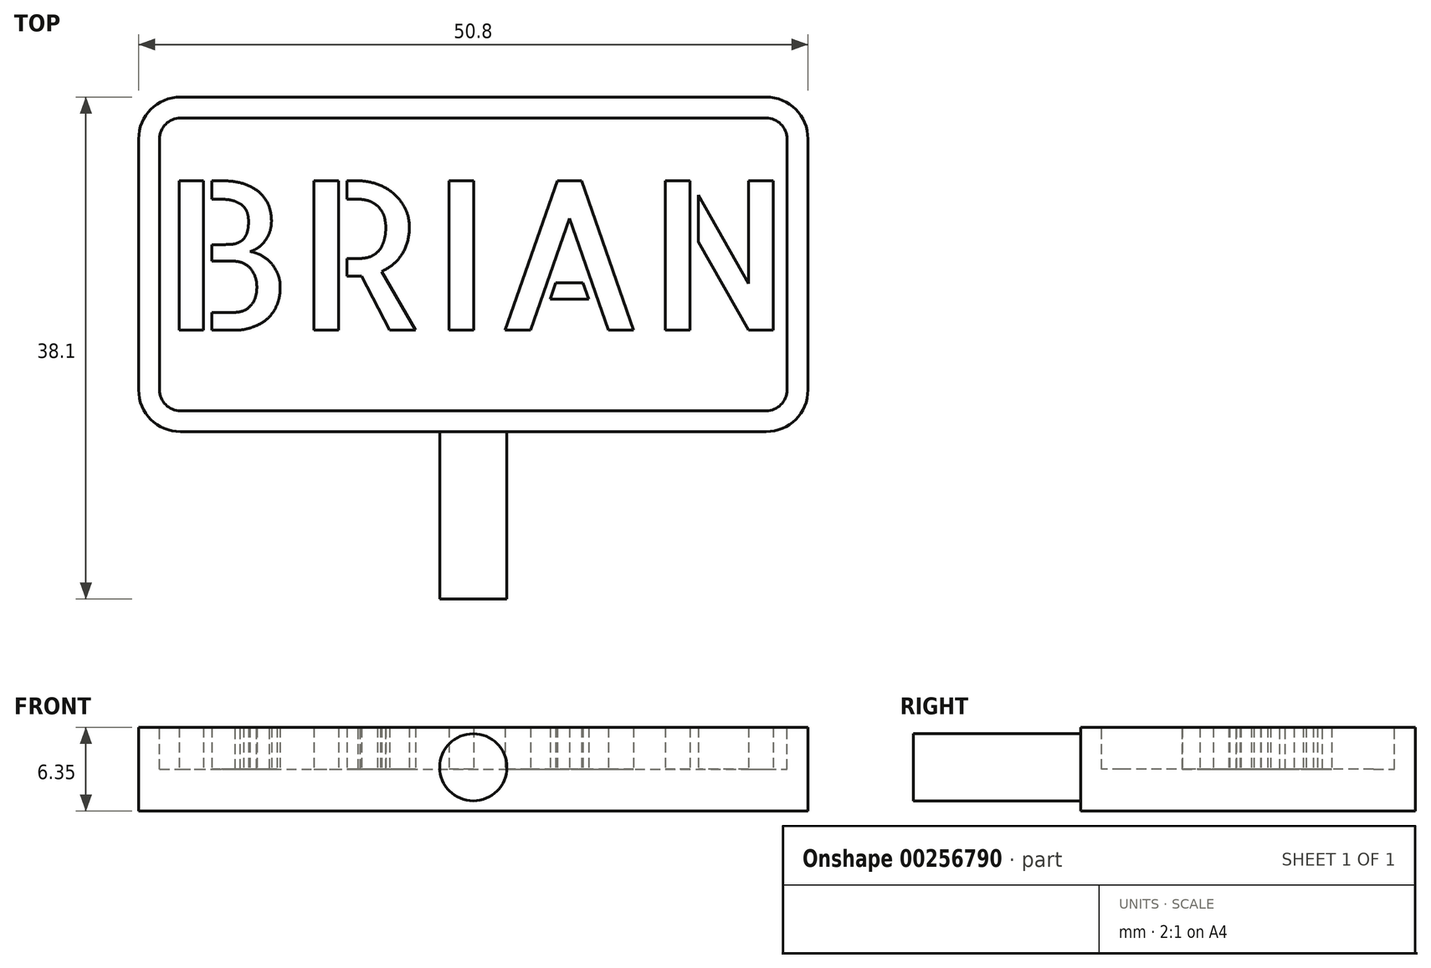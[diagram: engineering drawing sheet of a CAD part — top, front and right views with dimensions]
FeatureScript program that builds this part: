
annotation { "Feature Type Name" : "Feature", "Feature Type Description" : "" }
export const myFeature = defineFeature(function(context is Context, id is Id, definition is map)
    precondition{}
    {
        {
            var Q0;
            Q0=qCreatedBy(makeId("Top.planeOp"),FACE);
            var sketch = newSketch(context, id + "F0", { "sketchPlane" : qUnion([Q0])});
            skLineSegment(sketch, "E0.bottom", {"start": v(22.23, 12.7) * mm, "end": v(-22.23, 12.7) * mm});
            skLineSegment(sketch, "E0.top", {"start": v(22.23, -12.7) * mm, "end": v(-22.23, -12.7) * mm});
            skLineSegment(sketch, "E0.left", {"start": v(25.4, 9.53) * mm, "end": v(25.4, -9.53) * mm});
            skLineSegment(sketch, "E0.right", {"start": v(-25.4, 9.53) * mm, "end": v(-25.4, -9.53) * mm});
            skPoint(sketch, "E0.middle", {"position": v(0, 0) * mm});
            skPoint(sketch, "E1.visualSharp", {"position": v(-25.4, -12.7) * mm});
            skArc(sketch, "E1.filletArc", {"start": v(-25.4, -9.53) * mm, "mid": v(-24.47, -11.77) * mm, "end": v(-22.23, -12.7) * mm});
            skPoint(sketch, "E2.visualSharp", {"position": v(-25.4, 12.7) * mm});
            skArc(sketch, "E2.filletArc", {"start": v(-22.23, 12.7) * mm, "mid": v(-24.47, 11.77) * mm, "end": v(-25.4, 9.53) * mm});
            skPoint(sketch, "E3.visualSharp", {"position": v(25.4, 12.7) * mm});
            skArc(sketch, "E3.filletArc", {"start": v(25.4, 9.53) * mm, "mid": v(24.47, 11.77) * mm, "end": v(22.23, 12.7) * mm});
            skPoint(sketch, "E4.visualSharp", {"position": v(25.4, -12.7) * mm});
            skArc(sketch, "E4.filletArc", {"start": v(22.23, -12.7) * mm, "mid": v(24.47, -11.77) * mm, "end": v(25.4, -9.53) * mm});
            skSolve(sketch);
        }
        {
            var Q0;
            Q0=makeQuery(id+"F0.imprint","IMPRINT",FACE,{"disambiguationData":[TD([[makeQuery(id+"F0.imprint","IMPRINT",EDGE,{"derivedFrom":sQuery(id+"F0.wireOp",EDGE,"E0.bottom")}),1.0]])]});
            extrude(context, id + "F1", {"entities" : qUnion([Q0]), "depth" : 6.35 * mm});
        }
        {
            var Q0;
            Q0=makeQuery(id+"F1.opExtrude","CAP_FACE",FACE,{"disambiguationData":[OSD([sQuery(id+"F0.wireOp",EDGE,"E0.bottom"),sQuery(id+"F0.wireOp",EDGE,"E0.top"),sQuery(id+"F0.wireOp",EDGE,"E0.left"),sQuery(id+"F0.wireOp",EDGE,"E0.right"),sQuery(id+"F0.wireOp",EDGE,"E1.filletArc"),sQuery(id+"F0.wireOp",EDGE,"E2.filletArc"),sQuery(id+"F0.wireOp",EDGE,"E3.filletArc"),sQuery(id+"F0.wireOp",EDGE,"E4.filletArc")])],"isStart":false});
            var sketch = newSketch(context, id + "F2", { "sketchPlane" : qUnion([Q0])});
            skLineSegment(sketch, "E5.0", {"start": v(-22.22, -11.11) * mm, "end": v(22.22, -11.11) * mm});
            skLineSegment(sketch, "E5.1", {"start": v(-23.81, 9.52) * mm, "end": v(-23.81, -9.52) * mm});
            skLineSegment(sketch, "E5.2", {"start": v(22.22, 11.11) * mm, "end": v(-22.22, 11.11) * mm});
            skLineSegment(sketch, "E5.3", {"start": v(23.81, -9.52) * mm, "end": v(23.81, 9.52) * mm});
            skPoint(sketch, "E6.visualSharp", {"position": v(-23.81, 11.11) * mm});
            skArc(sketch, "E6.filletArc", {"start": v(-22.22, 11.11) * mm, "mid": v(-23.35, 10.65) * mm, "end": v(-23.81, 9.52) * mm});
            skPoint(sketch, "E7.visualSharp", {"position": v(-23.81, -11.11) * mm});
            skArc(sketch, "E7.filletArc", {"start": v(-23.81, -9.52) * mm, "mid": v(-23.35, -10.65) * mm, "end": v(-22.22, -11.11) * mm});
            skPoint(sketch, "E8.visualSharp", {"position": v(23.81, -11.11) * mm});
            skArc(sketch, "E8.filletArc", {"start": v(22.22, -11.11) * mm, "mid": v(23.35, -10.65) * mm, "end": v(23.81, -9.52) * mm});
            skPoint(sketch, "E9.visualSharp", {"position": v(23.81, 11.11) * mm});
            skArc(sketch, "E9.filletArc", {"start": v(23.81, 9.52) * mm, "mid": v(23.35, 10.65) * mm, "end": v(22.22, 11.11) * mm});
            skSolve(sketch);
        }
        {
            var Q0;
            Q0=makeQuery(id+"F2.imprint","IMPRINT",FACE,{"disambiguationData":[TD([[makeQuery(id+"F2.imprint","IMPRINT",EDGE,{"derivedFrom":sQuery(id+"F2.wireOp",EDGE,"E5.0")}),1.0]])]});
            extrude(context, id + "F3", {"entities" : qUnion([Q0]), "operationType" : NewBodyOperationType.REMOVE, "oppositeDirection" : true, "depth" : 3.17 * mm});
        }
        {
            var Q0;
            Q0=makeQuery(id+"F3.boolean.opBoolean","COPY",FACE,{"derivedFrom":makeQuery(id+"F3.opExtrude","CAP_FACE",FACE,{"disambiguationData":[OSD([sQuery(id+"F2.wireOp",EDGE,"E5.0"),sQuery(id+"F2.wireOp",EDGE,"E5.1"),sQuery(id+"F2.wireOp",EDGE,"E5.2"),sQuery(id+"F2.wireOp",EDGE,"E5.3"),sQuery(id+"F2.wireOp",EDGE,"E6.filletArc"),sQuery(id+"F2.wireOp",EDGE,"E7.filletArc"),sQuery(id+"F2.wireOp",EDGE,"E8.filletArc"),sQuery(id+"F2.wireOp",EDGE,"E9.filletArc")])],"isStart":false})});
            var sketch = newSketch(context, id + "F4", { "sketchPlane" : qUnion([Q0])});
            skText(sketch, "E10", { "text": "BRIAN", "fontName": "AllertaStencil-Regular.ttf"});
            const initialGuessF4  = {"E10": [-0.02381, -0.005, 1, 0, 0.01136]};
            skSetInitialGuess(sketch, initialGuessF4);
            skSolve(sketch);
        }
        {
            var Q0;
            Q0 = qSketchRegion(id + "F4", true);
            var Q1;
            Q1=makeQuery(id+"F1.opExtrude","CAP_FACE",FACE,{"disambiguationData":[OSD([sQuery(id+"F0.wireOp",EDGE,"E0.bottom"),sQuery(id+"F0.wireOp",EDGE,"E0.top"),sQuery(id+"F0.wireOp",EDGE,"E0.left"),sQuery(id+"F0.wireOp",EDGE,"E0.right"),sQuery(id+"F0.wireOp",EDGE,"E1.filletArc"),sQuery(id+"F0.wireOp",EDGE,"E2.filletArc"),sQuery(id+"F0.wireOp",EDGE,"E3.filletArc"),sQuery(id+"F0.wireOp",EDGE,"E4.filletArc")])],"isStart":false});
            extrude(context, id + "F5", {"entities" : qUnion([Q0]), "operationType" : NewBodyOperationType.ADD, "endBound" : BoundingType.UP_TO_SURFACE, "endBoundEntityFace" : qUnion([Q1]), "depth" : 25.4 * mm});
        }
        {
            var Q0;
            Q0=makeQuery(id+"F1.opExtrude","SWEPT_FACE",FACE,{"disambiguationData":[OSD([sQuery(id+"F0.wireOp",EDGE,"E0.top")])]});
            var sketch = newSketch(context, id + "F6", { "sketchPlane" : qUnion([Q0])});
            skCircle(sketch, "E11", {"center": v(0, 3.32) * mm, "radius": 2.55 * mm});
            skSolve(sketch);
        }
        {
            var Q0;
            Q0=makeQuery(id+"F6.imprint","IMPRINT",FACE,{"disambiguationData":[TD([[makeQuery(id+"F6.imprint","IMPRINT",EDGE,{"derivedFrom":sQuery(id+"F6.wireOp",EDGE,"E11")}),1.0]])]});
            var Q1;
            Q1=sQuery(id+"F6.wireOp",EDGE,"E11");
            extrude(context, id + "F7", {"entities" : qUnion([Q0]), "surfaceEntities" : qUnion([Q1]), "depth" : 12.7 * mm});
        }
    });
